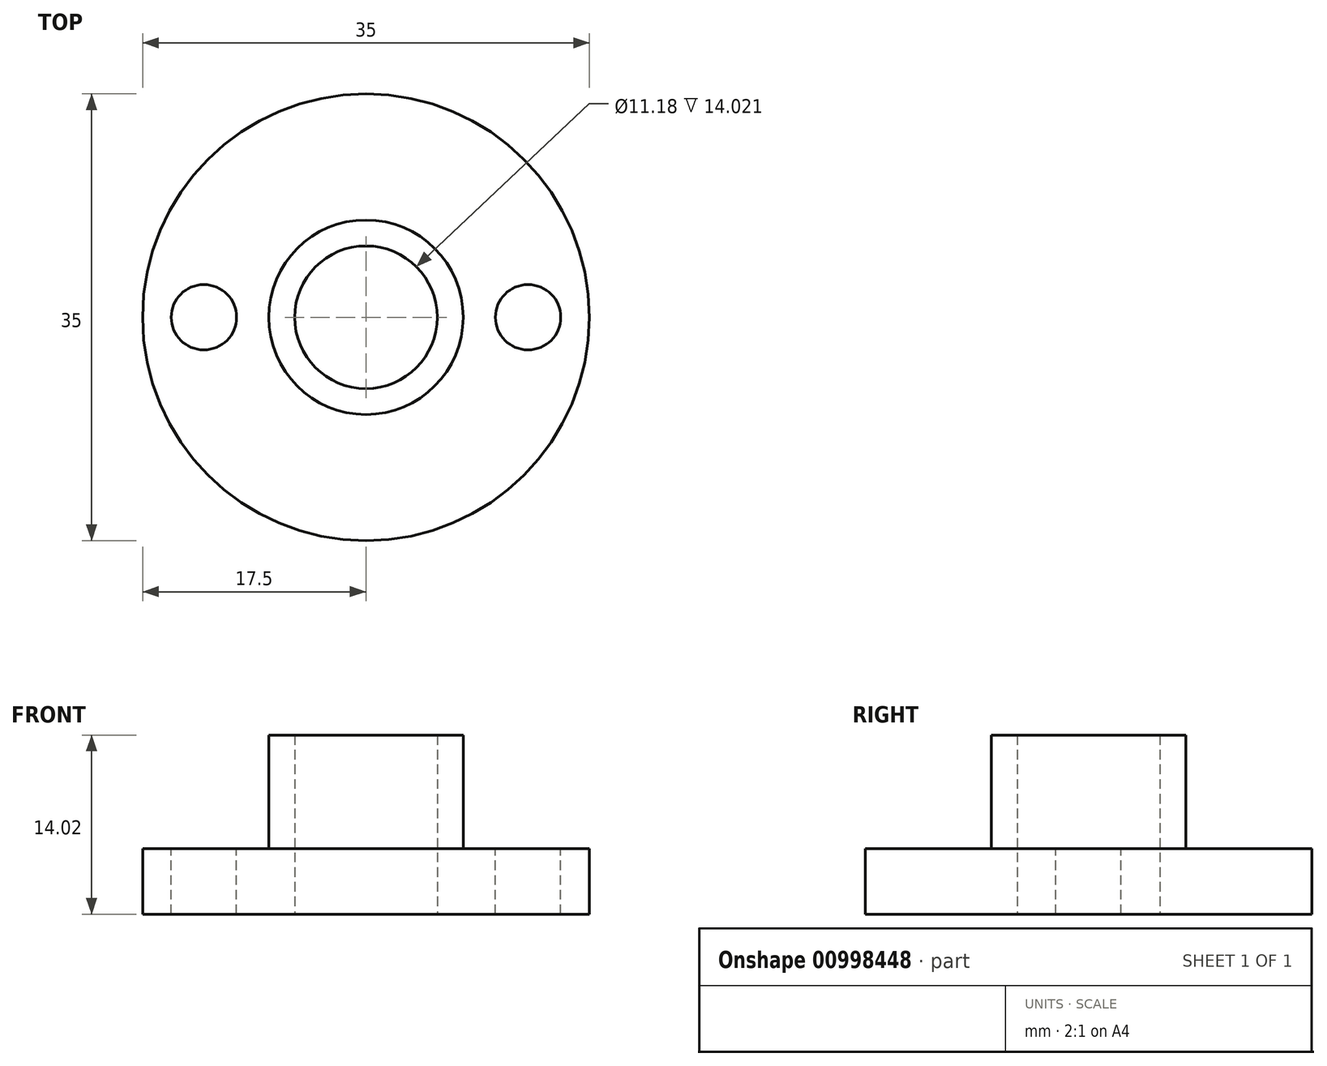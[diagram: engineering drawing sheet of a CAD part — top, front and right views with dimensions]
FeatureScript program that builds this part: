
annotation { "Feature Type Name" : "Feature", "Feature Type Description" : "" }
export const myFeature = defineFeature(function(context is Context, id is Id, definition is map)
    precondition{}
    {
        {
            var Q0;
            Q0=qCreatedBy(makeId("Top.planeOp"),FACE);
            var sketch = newSketch(context, id + "F0", { "sketchPlane" : qUnion([Q0])});
            skCircle(sketch, "E0", {"center": v(0, 0) * mm, "radius": 17.5 * mm});
            skSolve(sketch);
        }
        {
            var Q0;
            Q0 = qSketchRegion(id + "F0", true);
            extrude(context, id + "F1", {"entities" : qUnion([Q0]), "depth" : 5.13 * mm, "offsetDistance" : 25.4 * mm});
        }
        {
            var Q0;
            Q0=makeQuery(id+"F1.opExtrude","CAP_FACE",FACE,{"disambiguationData":[OSD([sQuery(id+"F0.wireOp",EDGE,"E0")])],"isStart":false});
            var sketch = newSketch(context, id + "F2", { "sketchPlane" : qUnion([Q0])});
            skCircle(sketch, "E1", {"center": v(0, 0) * mm, "radius": 5.59 * mm});
            skCircle(sketch, "E2", {"center": v(0, 0) * mm, "radius": 7.62 * mm});
            skSolve(sketch);
        }
        {
            var Q0;
            Q0 = qSketchRegion(id + "F2", true);
            extrude(context, id + "F3", {"entities" : qUnion([Q0]), "operationType" : NewBodyOperationType.ADD, "depth" : 8.9 * mm, "offsetDistance" : 25.4 * mm});
        }
        {
            var Q0;
            Q0=makeQuery(id+"F1.opExtrude","CAP_FACE",FACE,{"disambiguationData":[OSD([sQuery(id+"F0.wireOp",EDGE,"E0")])],"isStart":true});
            var sketch = newSketch(context, id + "F4", { "sketchPlane" : qUnion([Q0])});
            skCircle(sketch, "E3", {"center": v(0, 0) * mm, "radius": 5.59 * mm});
            skSolve(sketch);
        }
        {
            var Q0;
            Q0 = qSketchRegion(id + "F4", true);
            extrude(context, id + "F5", {"entities" : qUnion([Q0]), "operationType" : NewBodyOperationType.REMOVE, "endBound" : BoundingType.THROUGH_ALL, "oppositeDirection" : true, "depth" : 25.4 * mm, "offsetDistance" : 25.4 * mm});
        }
        {
            var Q0;
            {var subQ0=sQuery(id+"F0.wireOp",EDGE,"E0");Q0=makeQuery(id+"F3.boolean.opBoolean","SPLIT",FACE,{"disambiguationData":[TD([makeQuery(id+"F1.opExtrude","SWEPT_FACE",FACE,{"disambiguationData":[OSD([subQ0])]})])],"derivedFrom":makeQuery(id+"F1.opExtrude","CAP_FACE",FACE,{"disambiguationData":[OSD([subQ0])],"isStart":false})});}
            var sketch = newSketch(context, id + "F6", { "sketchPlane" : qUnion([Q0])});
            skPoint(sketch, "E4", {"position": v(-12.7, 0) * mm});
            skPoint(sketch, "E5", {"position": v(12.7, 0) * mm});
            skSolve(sketch);
        }
        {
            var Q0;
            Q0=sQuery(id+"F6.wireOp",VERTEX,"E4");
            var Q1;
            Q1=sQuery(id+"F6.wireOp",VERTEX,"E5");
            var Q2;
            Q2=makeQuery(id+"F1.opExtrude","SWEPT_BODY",BODY,{"disambiguationData":[OSD([sQuery(id+"F0.wireOp",EDGE,"E0")])]});
            hole(context, id + "F7", {"style" : HoleStyle.SIMPLE, "endStyle" : HoleEndStyle.THROUGH, "holeDiameter" : 5.12 * mm, "majorDiameter" : 6.35 * mm, "isTappedThrough" : true, "tappedDepth" : 12.7 * mm, "tapClearance" : 3, "locations" : qUnion([Q0, Q1]), "scope" : qUnion([Q2])});
        }
    });
